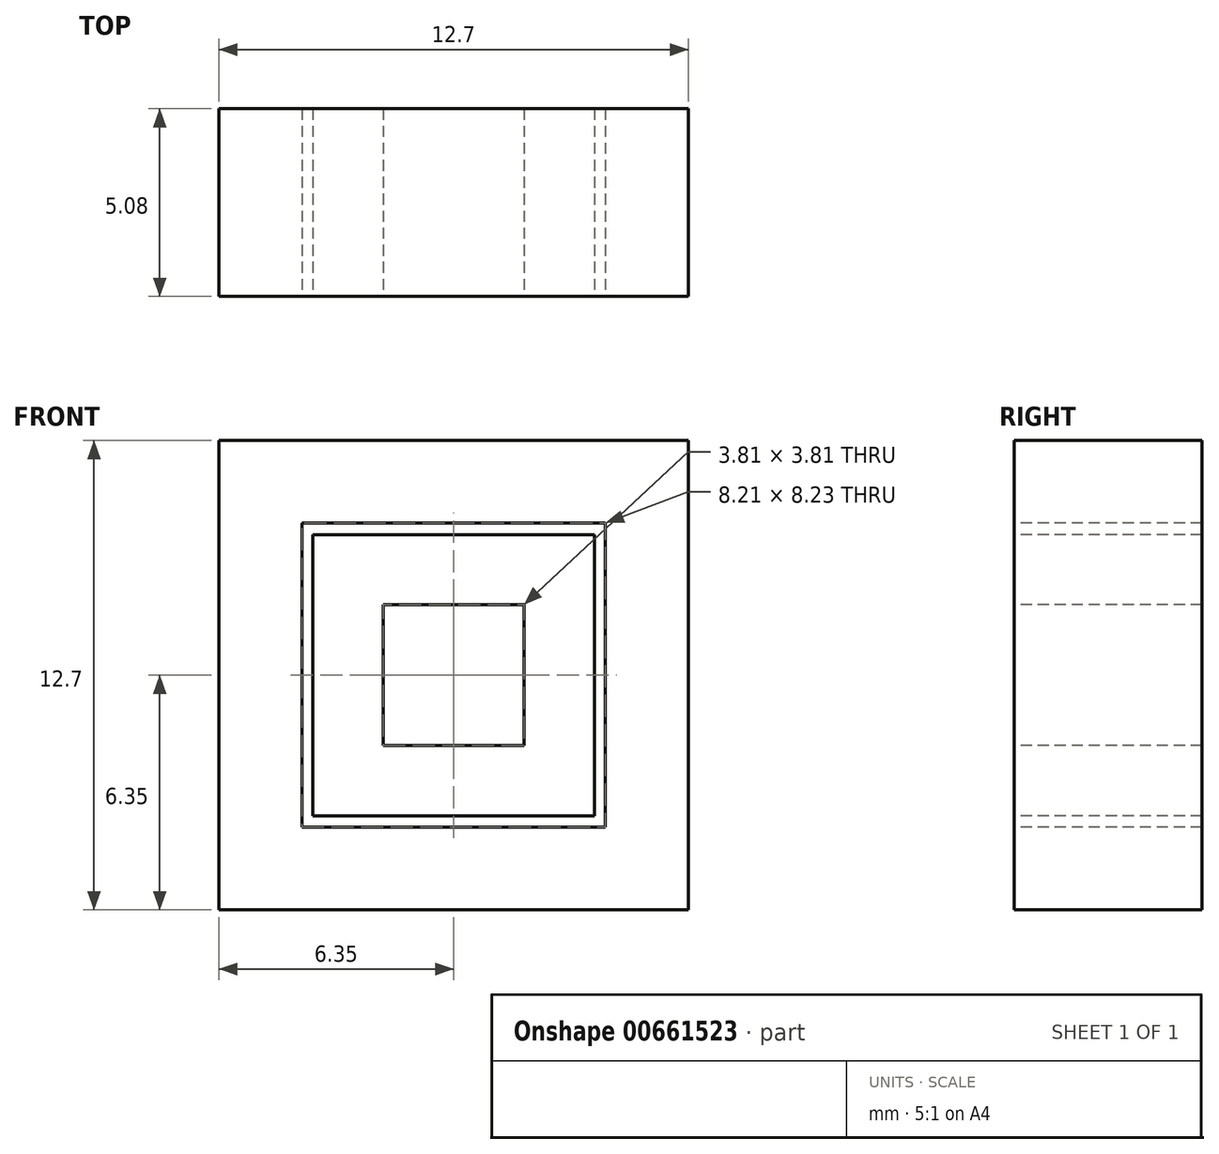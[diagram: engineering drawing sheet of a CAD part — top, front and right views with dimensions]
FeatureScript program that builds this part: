
annotation { "Feature Type Name" : "Feature", "Feature Type Description" : "" }
export const myFeature = defineFeature(function(context is Context, id is Id, definition is map)
    precondition{}
    {
        {
            var Q0;
            Q0=qCreatedBy(makeId("Front.planeOp"),FACE);
            var sketch = newSketch(context, id + "F0", { "sketchPlane" : qUnion([Q0])});
            skLineSegment(sketch, "E0.bottom", {"start": v(-6.35, 6.35) * mm, "end": v(6.35, 6.35) * mm});
            skLineSegment(sketch, "E0.top", {"start": v(-6.35, -6.35) * mm, "end": v(6.35, -6.35) * mm});
            skLineSegment(sketch, "E0.left", {"start": v(-6.35, 6.35) * mm, "end": v(-6.35, -6.35) * mm});
            skLineSegment(sketch, "E0.right", {"start": v(6.35, 6.35) * mm, "end": v(6.35, -6.35) * mm});
            skPoint(sketch, "E0.middle", {"position": v(0, 0) * mm});
            skSolve(sketch);
        }
        {
            var Q0;
            Q0=makeQuery(id+"F0.imprint","IMPRINT",FACE,{"disambiguationData":[TD([[makeQuery(id+"F0.imprint","IMPRINT",EDGE,{"derivedFrom":sQuery(id+"F0.wireOp",EDGE,"E0.bottom")}),-1.0]])]});
            extrude(context, id + "F1", {"entities" : qUnion([Q0]), "depth" : 5.08 * mm, "offsetDistance" : 25.4 * mm});
        }
        {
            var Q0;
            Q0=makeQuery(id+"F1.opExtrude","CAP_FACE",FACE,{"disambiguationData":[OSD([sQuery(id+"F0.wireOp",EDGE,"E0.bottom"),sQuery(id+"F0.wireOp",EDGE,"E0.top"),sQuery(id+"F0.wireOp",EDGE,"E0.left"),sQuery(id+"F0.wireOp",EDGE,"E0.right")])],"isStart":false});
            var sketch = newSketch(context, id + "F2", { "sketchPlane" : qUnion([Q0])});
            skLineSegment(sketch, "E1.bottom", {"start": v(-3.82, 3.8) * mm, "end": v(3.82, 3.8) * mm});
            skLineSegment(sketch, "E1.top", {"start": v(-3.82, -3.8) * mm, "end": v(3.82, -3.8) * mm});
            skLineSegment(sketch, "E1.left", {"start": v(-3.82, 3.8) * mm, "end": v(-3.82, -3.8) * mm});
            skLineSegment(sketch, "E1.right", {"start": v(3.82, 3.8) * mm, "end": v(3.82, -3.8) * mm});
            skPoint(sketch, "E1.middle", {"position": v(0, 0) * mm});
            skSolve(sketch);
        }
        {
            var Q0;
            Q0=makeQuery(id+"F2.imprint","IMPRINT",FACE,{"disambiguationData":[TD([[makeQuery(id+"F2.imprint","IMPRINT",EDGE,{"derivedFrom":sQuery(id+"F2.wireOp",EDGE,"E1.bottom")}),-1.0]])]});
            var sketch = newSketch(context, id + "F3", { "sketchPlane" : qUnion([Q0])});
            skLineSegment(sketch, "E2.bottom", {"start": v(-1.9, 1.9) * mm, "end": v(1.9, 1.9) * mm});
            skLineSegment(sketch, "E2.top", {"start": v(-1.9, -1.9) * mm, "end": v(1.9, -1.9) * mm});
            skLineSegment(sketch, "E2.left", {"start": v(-1.9, 1.9) * mm, "end": v(-1.9, -1.9) * mm});
            skLineSegment(sketch, "E2.right", {"start": v(1.9, 1.9) * mm, "end": v(1.9, -1.9) * mm});
            skPoint(sketch, "E2.middle", {"position": v(0, 0) * mm});
            skSolve(sketch);
        }
        {
            var Q0;
            Q0=makeQuery(id+"F2.imprint","IMPRINT",FACE,{"disambiguationData":[TD([[makeQuery(id+"F2.imprint","IMPRINT",EDGE,{"derivedFrom":sQuery(id+"F2.wireOp",EDGE,"E1.bottom")}),1.0]])]});
            var sketch = newSketch(context, id + "F4", { "sketchPlane" : qUnion([Q0])});
            skLineSegment(sketch, "E3.bottom", {"start": v(-4.1, 4.11) * mm, "end": v(4.1, 4.11) * mm});
            skLineSegment(sketch, "E3.top", {"start": v(-4.1, -4.11) * mm, "end": v(4.1, -4.11) * mm});
            skLineSegment(sketch, "E3.left", {"start": v(-4.1, 4.11) * mm, "end": v(-4.1, -4.11) * mm});
            skLineSegment(sketch, "E3.right", {"start": v(4.1, 4.11) * mm, "end": v(4.1, -4.11) * mm});
            skPoint(sketch, "E3.middle", {"position": v(0, 0) * mm});
            skSolve(sketch);
        }
        {
            var Q0;
            Q0=makeQuery(id+"F3.imprint","IMPRINT",FACE,{"disambiguationData":[TD([[makeQuery(id+"F3.imprint","IMPRINT",EDGE,{"derivedFrom":sQuery(id+"F3.wireOp",EDGE,"E2.bottom")}),-1.0]])]});
            extrude(context, id + "F5", {"entities" : qUnion([Q0]), "operationType" : NewBodyOperationType.REMOVE, "oppositeDirection" : true, "depth" : 25.4 * mm, "offsetDistance" : 25.4 * mm});
        }
        {
            var Q0;
            Q0=makeQuery(id+"F4.imprint","IMPRINT",FACE,{"disambiguationData":[TD([[makeQuery(id+"F4.imprint","IMPRINT",EDGE,{"derivedFrom":sQuery(id+"F4.wireOp",EDGE,"E3.bottom")}),-1.0]])]});
            extrude(context, id + "F6", {"entities" : qUnion([Q0]), "operationType" : NewBodyOperationType.REMOVE, "oppositeDirection" : true, "depth" : 25.4 * mm, "offsetDistance" : 25.4 * mm});
        }
    });
